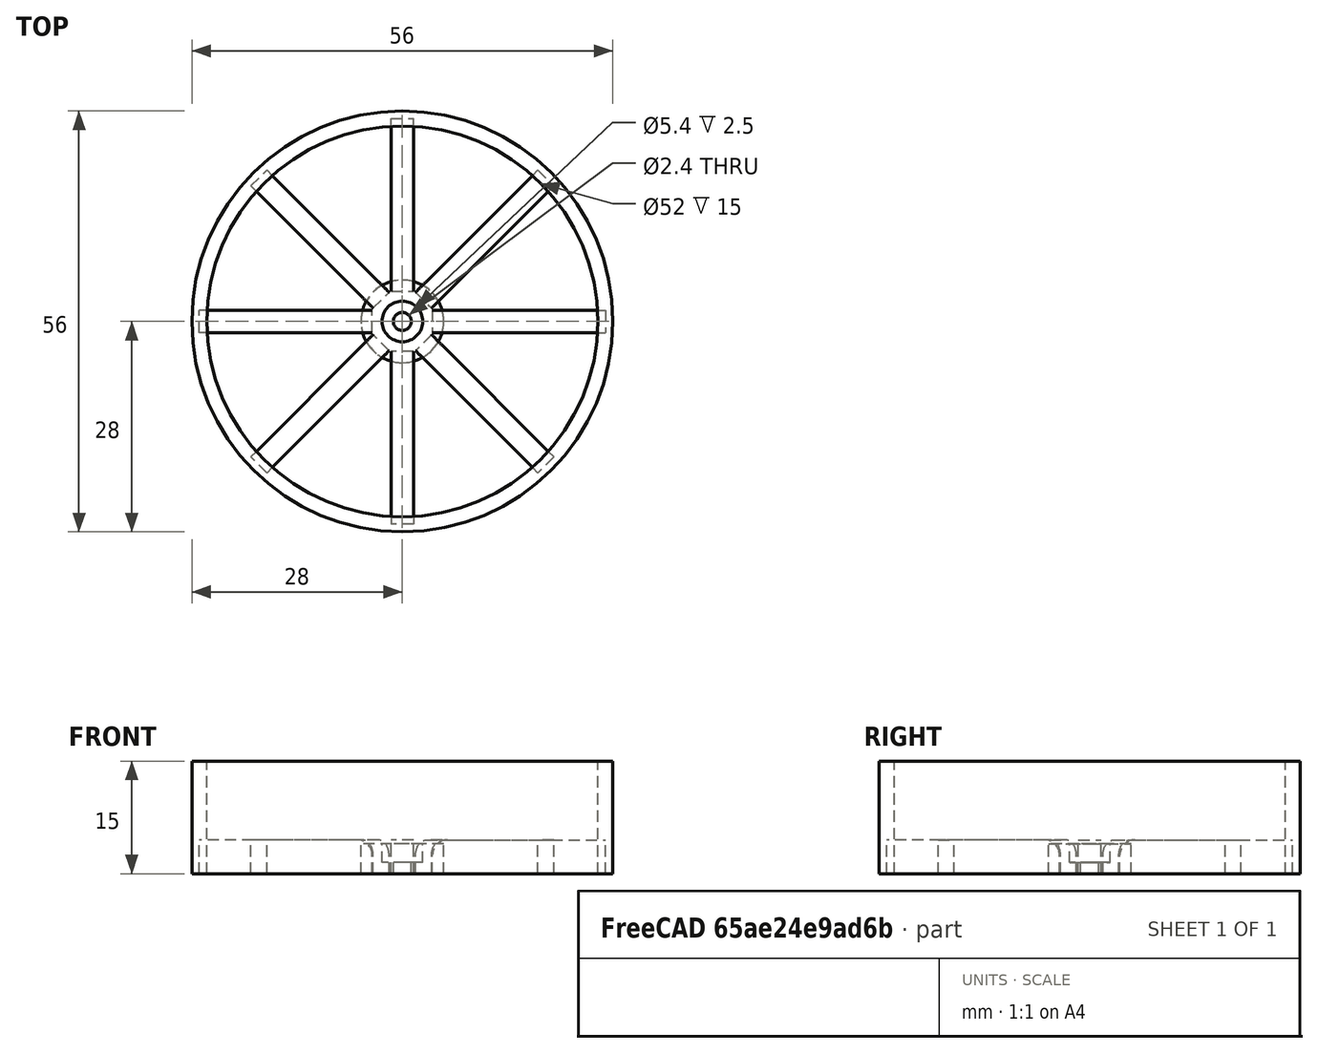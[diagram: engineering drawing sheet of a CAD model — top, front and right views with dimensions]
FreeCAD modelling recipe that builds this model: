
FCSTD DOCUMENT  (FreeCAD 0.16R6712 (Git))
Label: roda_carro
License: All rights reserved
LicenseURL: http://en.wikipedia.org/wiki/All_rights_reserved
objects: Part::Box×8, Part::Fillet×8, Part::Cylinder×5, Part::Cut×3
note: 24 computed .brp shape members not serialized (recipe doc carries the construction recipe); baked Part::Feature solids carry a one-line shape summary decoded from their .brp

FEATURE [Part::Cylinder] Cylinder  label="gross"
  Angle = 360
  Height = 4
  Placement = pos=(0,0,-1) rot=(0,0,1;0rad)
  Radius = 5.5
FEATURE [Part::Cylinder] Cylinder001  label="interior"
  Angle = 360
  Height = 6
  Placement = pos=(0,0,0.5) rot=(0,0,1;0rad)
  Radius = 2.7
FEATURE [Part::Cylinder] Cylinder002  label="Cylinder"
  Angle = 360
  Height = 7
  Placement = pos=(0,0,-1) rot=(0,0,1;0rad)
  Radius = 1.2
FEATURE [Part::Cut] Cut
  Base = -> Cylinder
  Tool = -> Cylinder002
FEATURE [Part::Cut] Cut001
  Base = -> Cut
  Placement = pos=(0,0,1) rot=(0,0,1;0rad)
  Tool = -> Cylinder001
FEATURE [Part::Cylinder] Cylinder004  label="fora_gran"
  Angle = 360
  Height = 15
  Placement = pos=(0,0,1) rot=(0,0,1;0rad)
  Radius = 28
FEATURE [Part::Cylinder] Cylinder005  label="forat_gran"
  Angle = 360
  Height = 15
  Placement = pos=(0,0,1) rot=(0,0,1;0rad)
  Radius = 26
FEATURE [Part::Box] Box  label="Cube"
  Height = 4.5
  Length = 3
  Placement = pos=(-1.5,4,0) rot=(0,0,1;0rad)
  Width = 23
FEATURE [Part::Cut] Cut002
  Base = -> Cylinder004
  Placement = pos=(0,0,-1) rot=(0,0,1;0rad)
  Tool = -> Cylinder005
FEATURE [Part::Fillet] Fillet
  Base = -> Box
  Edges = 1 edges r=2: [Edge10]
FEATURE [Part::Box] Box001  label="Cube001"
  Height = 4.5
  Length = 3
  Placement = pos=(-4,-1.5,0) rot=(0,0,1;1.5708rad)
  Width = 23
FEATURE [Part::Fillet] Fillet001
  Base = -> Box001
  Edges = 1 edges r=2: [Edge10]
FEATURE [Part::Box] Box002  label="Cube002"
  Height = 4.5
  Length = 3
  Placement = pos=(-4,-1.5,0) rot=(0,0,1;1.5708rad)
  Width = 23
FEATURE [Part::Fillet] Fillet002
  Base = -> Box002
  Edges = 1 edges r=2: [Edge10]
  Placement = pos=(0,0,0) rot=(0,0,1;3.14159rad)
FEATURE [Part::Box] Box003  label="Cube003"
  Height = 4.5
  Length = 3
  Placement = pos=(-1.5,4,0) rot=(0,0,1;0rad)
  Width = 23
FEATURE [Part::Fillet] Fillet003
  Base = -> Box003
  Edges = 1 edges r=2: [Edge10]
  Placement = pos=(0,0,0) rot=(0,0,1;3.14159rad)
FEATURE [Part::Box] Box004  label="Cube004"
  Height = 4.5
  Length = 3
  Placement = pos=(-4,-1.5,0) rot=(0,0,1;1.5708rad)
  Width = 23
FEATURE [Part::Fillet] Fillet004
  Base = -> Box004
  Edges = 1 edges r=2: [Edge10]
  Placement = pos=(0,0,0) rot=(0,0,1;0.785398rad)
FEATURE [Part::Box] Box005  label="Cube005"
  Height = 4.5
  Length = 3
  Placement = pos=(-4,-1.5,0) rot=(0,0,1;1.5708rad)
  Width = 23
FEATURE [Part::Fillet] Fillet005
  Base = -> Box005
  Edges = 1 edges r=2: [Edge10]
  Placement = pos=(0,0,0) rot=(0,0,1;2.35619rad)
FEATURE [Part::Box] Box006  label="Cube006"
  Height = 4.5
  Length = 3
  Placement = pos=(-4,-1.5,0) rot=(0,0,1;1.5708rad)
  Width = 23
FEATURE [Part::Fillet] Fillet006
  Base = -> Box006
  Edges = 1 edges r=2: [Edge10]
  Placement = pos=(0,0,0) rot=(0,0,1;3.92699rad)
FEATURE [Part::Box] Box007  label="Cube007"
  Height = 4.5
  Length = 3
  Placement = pos=(-4,-1.5,0) rot=(0,0,1;1.5708rad)
  Width = 23
FEATURE [Part::Fillet] Fillet007
  Base = -> Box007
  Edges = 1 edges r=2: [Edge10]
  Placement = pos=(0,0,0) rot=(0,0,-1;0.785398rad)
